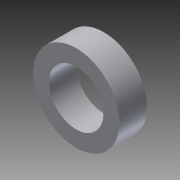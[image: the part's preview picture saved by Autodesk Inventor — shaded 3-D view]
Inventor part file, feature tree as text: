
AUTODESK INVENTOR PART (.ipt)
format: ipt  version: 2014 (Build 180170000, 170)  size: 84,992 bytes
history: native  units: in
note: dims shown in document units (in); Inventor stores cm internally (conversion verified against a paired STEP export)
features: extrude x1
ambient origin geometry x8: Origin, YZ Plane, XZ Plane, XY Plane, X Axis, Y Axis, Z Axis, Center Point
bodies: Solid1 (feature_tree)
feature tree (1):
  extrude  "Extrusion1"  Depth=0.63in
